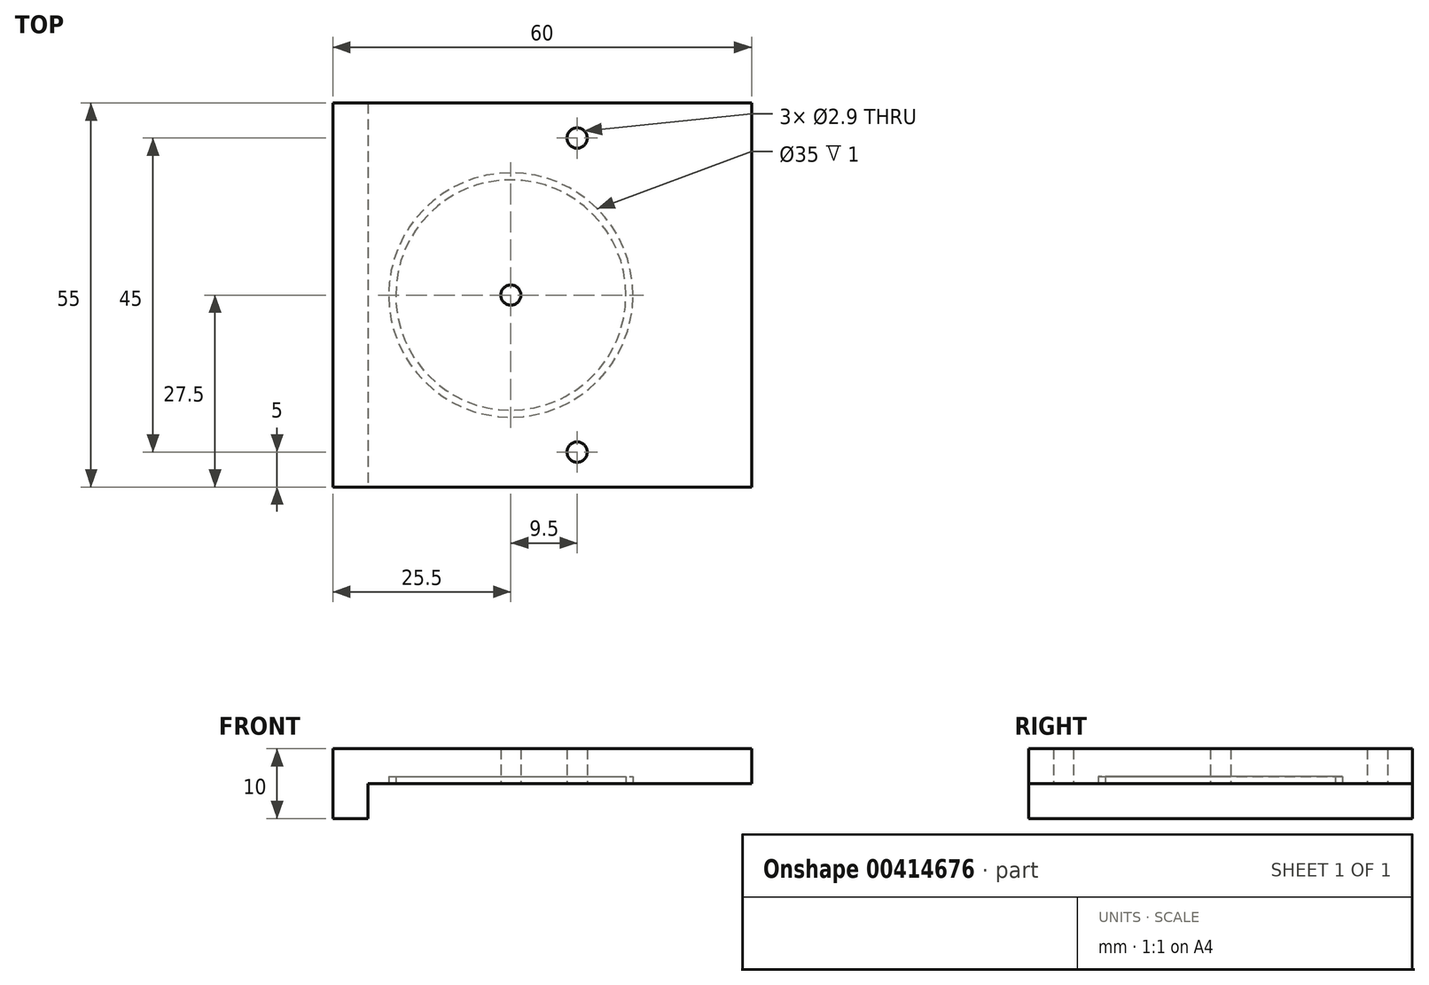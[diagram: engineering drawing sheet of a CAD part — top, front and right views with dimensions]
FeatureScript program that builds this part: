
annotation { "Feature Type Name" : "Feature", "Feature Type Description" : "" }
export const myFeature = defineFeature(function(context is Context, id is Id, definition is map)
    precondition{}
    {
        {
            var Q0;
            Q0=qCreatedBy(makeId("Top.planeOp"),FACE);
            var sketch = newSketch(context, id + "F0", { "sketchPlane" : qUnion([Q0])});
            skLineSegment(sketch, "E0.bottom", {"start": v(27.5, 27.5) * mm, "end": v(-27.5, 27.5) * mm});
            skLineSegment(sketch, "E0.top", {"start": v(27.5, -27.5) * mm, "end": v(-27.5, -27.5) * mm});
            skLineSegment(sketch, "E0.left", {"start": v(27.5, 27.5) * mm, "end": v(27.5, -27.5) * mm});
            skLineSegment(sketch, "E0.right", {"start": v(-27.5, 27.5) * mm, "end": v(-27.5, -27.5) * mm});
            skPoint(sketch, "E0.middle", {"position": v(0, 0) * mm});
            skCircle(sketch, "E1", {"center": v(-7, 0) * mm, "radius": 17.5 * mm});
            skLineSegment(sketch, "E2", {"start": v(2.5, 62.66) * mm, "end": v(2.5, -49.85) * mm, "construction": true});
            skCircle(sketch, "E3", {"center": v(2.5, 22.5) * mm, "radius": 1.45 * mm});
            skCircle(sketch, "E4", {"center": v(2.5, -22.5) * mm, "radius": 1.45 * mm});
            skCircle(sketch, "E5", {"center": v(-7, 0) * mm, "radius": 1.45 * mm});
            skSolve(sketch);
        }
        {
            var Q0;
            Q0=makeQuery(id+"F0.imprint","IMPRINT",FACE,{"disambiguationData":[TD([[makeQuery(id+"F0.imprint","IMPRINT",EDGE,{"derivedFrom":sQuery(id+"F0.wireOp",EDGE,"E0.bottom")}),1.0]])]});
            var Q1;
            Q1=makeQuery(id+"F0.imprint","IMPRINT",FACE,{"disambiguationData":[TD([[makeQuery(id+"F0.imprint","IMPRINT",EDGE,{"derivedFrom":sQuery(id+"F0.wireOp",EDGE,"E1")}),1.0]])]});
            extrude(context, id + "F1", {"entities" : qUnion([Q0, Q1]), "depth" : 5 * mm});
        }
        {
            var Q0;
            Q0=makeQuery(id+"F1.opExtrude","CAP_FACE",FACE,{"disambiguationData":[OSD([sQuery(id+"F0.wireOp",EDGE,"E0.bottom"),sQuery(id+"F0.wireOp",EDGE,"E0.top"),sQuery(id+"F0.wireOp",EDGE,"E0.left"),sQuery(id+"F0.wireOp",EDGE,"E0.right"),sQuery(id+"F0.wireOp",EDGE,"E3"),sQuery(id+"F0.wireOp",EDGE,"E4"),sQuery(id+"F0.wireOp",EDGE,"E5")])],"isStart":true});
            var sketch = newSketch(context, id + "F2", { "sketchPlane" : qUnion([Q0])});
            skCircle(sketch, "E6", {"center": v(-7, 0) * mm, "radius": 17.5 * mm});
            skCircle(sketch, "E7", {"center": v(-7, 0) * mm, "radius": 16.5 * mm});
            skSolve(sketch);
        }
        {
            var Q0;
            Q0=makeQuery(id+"F2.imprint","IMPRINT",FACE,{"disambiguationData":[TD([[makeQuery(id+"F2.imprint","IMPRINT",EDGE,{"derivedFrom":sQuery(id+"F2.wireOp",EDGE,"E6")}),1.0]])]});
            extrude(context, id + "F3", {"entities" : qUnion([Q0]), "operationType" : NewBodyOperationType.REMOVE, "oppositeDirection" : true, "depth" : 1 * mm});
        }
        {
            var Q0;
            Q0=makeQuery(id+"F1.opExtrude","CAP_FACE",FACE,{"disambiguationData":[OSD([sQuery(id+"F0.wireOp",EDGE,"E0.bottom"),sQuery(id+"F0.wireOp",EDGE,"E0.top"),sQuery(id+"F0.wireOp",EDGE,"E0.left"),sQuery(id+"F0.wireOp",EDGE,"E0.right"),sQuery(id+"F0.wireOp",EDGE,"E3"),sQuery(id+"F0.wireOp",EDGE,"E4"),sQuery(id+"F0.wireOp",EDGE,"E5")])],"isStart":false});
            var sketch = newSketch(context, id + "F4", { "sketchPlane" : qUnion([Q0])});
            skLineSegment(sketch, "E8.bottom", {"start": v(-27.5, -27.5) * mm, "end": v(-32.5, -27.5) * mm});
            skLineSegment(sketch, "E8.top", {"start": v(-27.5, 27.5) * mm, "end": v(-32.5, 27.5) * mm});
            skLineSegment(sketch, "E8.left", {"start": v(-27.5, -27.5) * mm, "end": v(-27.5, 27.5) * mm});
            skLineSegment(sketch, "E8.right", {"start": v(-32.5, -27.5) * mm, "end": v(-32.5, 27.5) * mm});
            skSolve(sketch);
        }
        {
            var Q0;
            Q0=makeQuery(id+"F4.imprint","IMPRINT",FACE,{"disambiguationData":[TD([[makeQuery(id+"F4.imprint","IMPRINT",EDGE,{"derivedFrom":sQuery(id+"F4.wireOp",EDGE,"E8.bottom")}),-1.0]])]});
            extrude(context, id + "F5", {"entities" : qUnion([Q0]), "operationType" : NewBodyOperationType.ADD, "oppositeDirection" : true, "depth" : 10 * mm});
        }
    });
